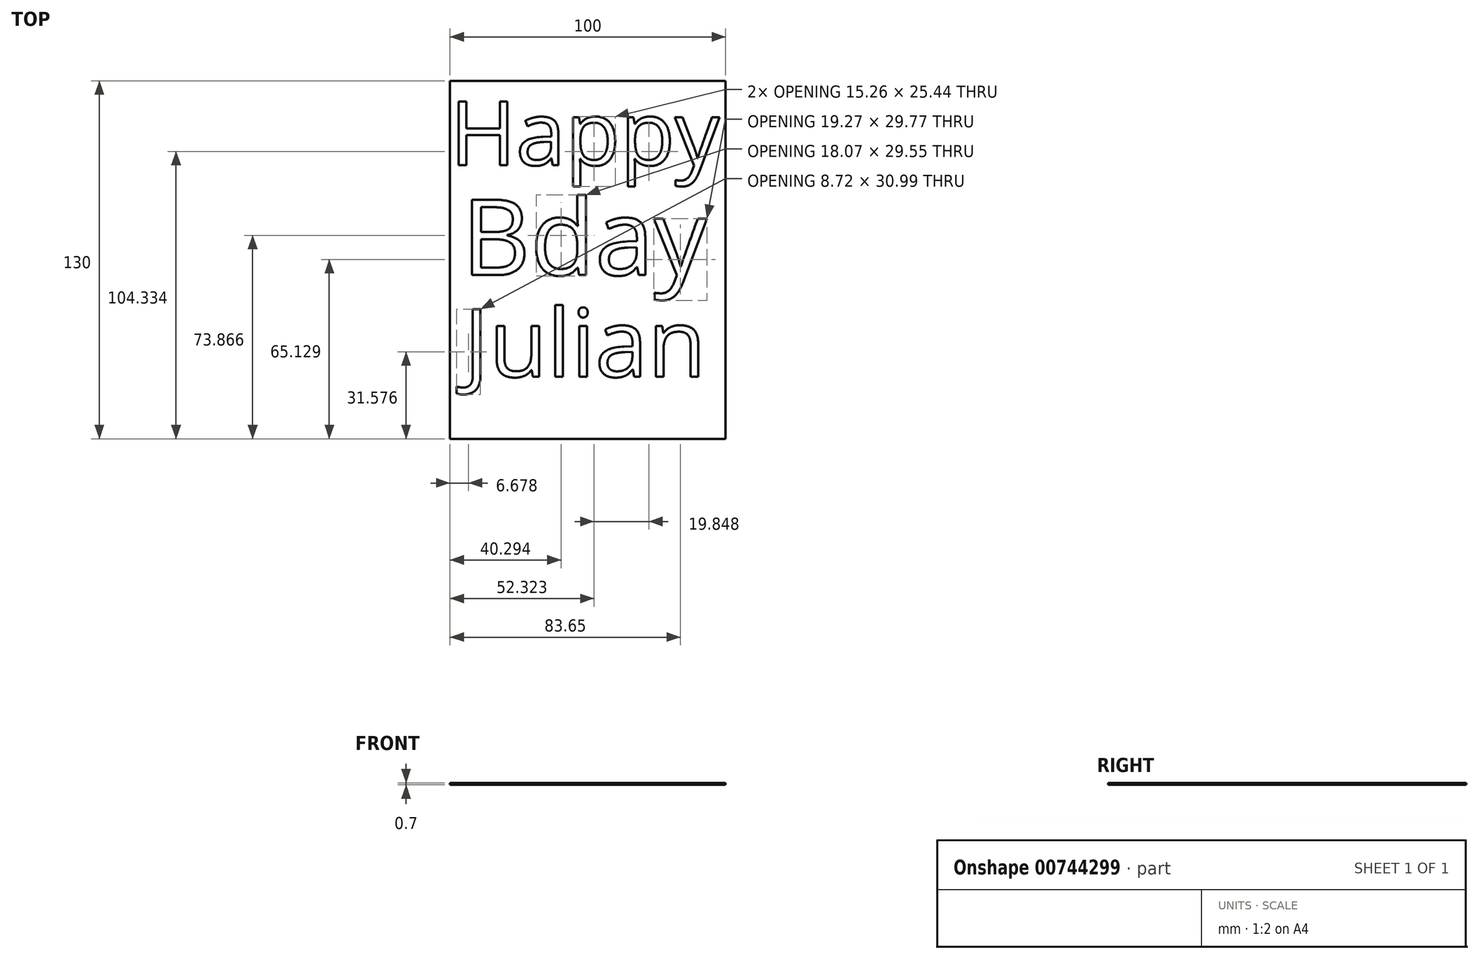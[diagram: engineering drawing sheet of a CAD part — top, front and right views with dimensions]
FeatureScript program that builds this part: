
annotation { "Feature Type Name" : "Feature", "Feature Type Description" : "" }
export const myFeature = defineFeature(function(context is Context, id is Id, definition is map)
    precondition{}
    {
        {
            var Q0;
            Q0=qCreatedBy(makeId("Top.planeOp"),FACE);
            var sketch = newSketch(context, id + "F0", { "sketchPlane" : qUnion([Q0])});
            skLineSegment(sketch, "E0.bottom", {"start": v(50, 65) * mm, "end": v(-50, 65) * mm});
            skLineSegment(sketch, "E0.top", {"start": v(50, -65) * mm, "end": v(-50, -65) * mm});
            skLineSegment(sketch, "E0.left", {"start": v(50, 65) * mm, "end": v(50, -65) * mm});
            skLineSegment(sketch, "E0.right", {"start": v(-50, 65) * mm, "end": v(-50, -65) * mm});
            skPoint(sketch, "E0.middle", {"position": v(0, 0) * mm});
            skSolve(sketch);
        }
        {
            var Q0;
            Q0=makeQuery(id+"F0.imprint","IMPRINT",FACE,{"disambiguationData":[TD([[makeQuery(id+"F0.imprint","IMPRINT",EDGE,{"derivedFrom":sQuery(id+"F0.wireOp",EDGE,"E0.bottom")}),1.0]])]});
            extrude(context, id + "F1", {"entities" : qUnion([Q0]), "depth" : .7 * mm, "offsetDistance" : 25 * mm});
        }
        {
            var Q0;
            Q0=makeQuery(id+"F1.opExtrude","CAP_FACE",FACE,{"disambiguationData":[OSD([sQuery(id+"F0.wireOp",EDGE,"E0.bottom"),sQuery(id+"F0.wireOp",EDGE,"E0.top"),sQuery(id+"F0.wireOp",EDGE,"E0.left"),sQuery(id+"F0.wireOp",EDGE,"E0.right")])],"isStart":false});
            var sketch = newSketch(context, id + "F2", { "sketchPlane" : qUnion([Q0])});
            skText(sketch, "E1", { "text": "Happy", "fontName": "OpenSans-Regular.ttf"});
            const initialGuessF2  = {"E1": [-0.05, 0.0344, 1, 0, 0.02332]};
            skSetInitialGuess(sketch, initialGuessF2);
            skSolve(sketch);
        }
        {
            var Q0;
            Q0=makeQuery(id+"F2.imprint","IMPRINT",FACE,{"disambiguationData":[TD([[makeQuery(id+"F2.imprint","IMPRINT",EDGE,{"derivedFrom":sQuery(id+"F2.wireOp",EDGE,"E1.sketch_text.stroke-0")}),1.0]])]});
            var sketch = newSketch(context, id + "F3", { "sketchPlane" : qUnion([Q0])});
            skText(sketch, "E2", { "text": "Bday", "fontName": "OpenSans-Regular.ttf"});
            const initialGuessF3  = {"E2": [-0.04577, -0.00553, 1, 0, 0.02764]};
            skSetInitialGuess(sketch, initialGuessF3);
            skSolve(sketch);
        }
        {
            var Q0;
            Q0=makeQuery(id+"F2.imprint","IMPRINT",FACE,{"disambiguationData":[TD([[makeQuery(id+"F2.imprint","IMPRINT",EDGE,{"derivedFrom":sQuery(id+"F2.wireOp",EDGE,"E1.sketch_text.stroke-0")}),1.0]])]});
            var sketch = newSketch(context, id + "F4", { "sketchPlane" : qUnion([Q0])});
            skText(sketch, "E3", { "text": "Julian", "fontName": "OpenSans-Regular.ttf"});
            const initialGuessF4  = {"E3": [-0.045, -0.04246, 1, 0, 0.02474]};
            skSetInitialGuess(sketch, initialGuessF4);
            skSolve(sketch);
        }
        {
            var Q0;
            Q0 = qSketchRegion(id + "F2", true);
            extrude(context, id + "F5", {"entities" : qUnion([Q0]), "operationType" : NewBodyOperationType.REMOVE, "endBound" : BoundingType.THROUGH_ALL, "oppositeDirection" : true, "depth" : 25 * mm, "offsetDistance" : 25 * mm});
        }
        {
            var Q0;
            Q0 = qSketchRegion(id + "F3", true);
            extrude(context, id + "F6", {"entities" : qUnion([Q0]), "operationType" : NewBodyOperationType.REMOVE, "endBound" : BoundingType.THROUGH_ALL, "oppositeDirection" : true, "depth" : 25 * mm, "offsetDistance" : 25 * mm});
        }
        {
            var Q0;
            Q0 = qSketchRegion(id + "F4", true);
            extrude(context, id + "F7", {"entities" : qUnion([Q0]), "operationType" : NewBodyOperationType.REMOVE, "endBound" : BoundingType.THROUGH_ALL, "oppositeDirection" : true, "depth" : 25 * mm, "offsetDistance" : 25 * mm});
        }
    });
